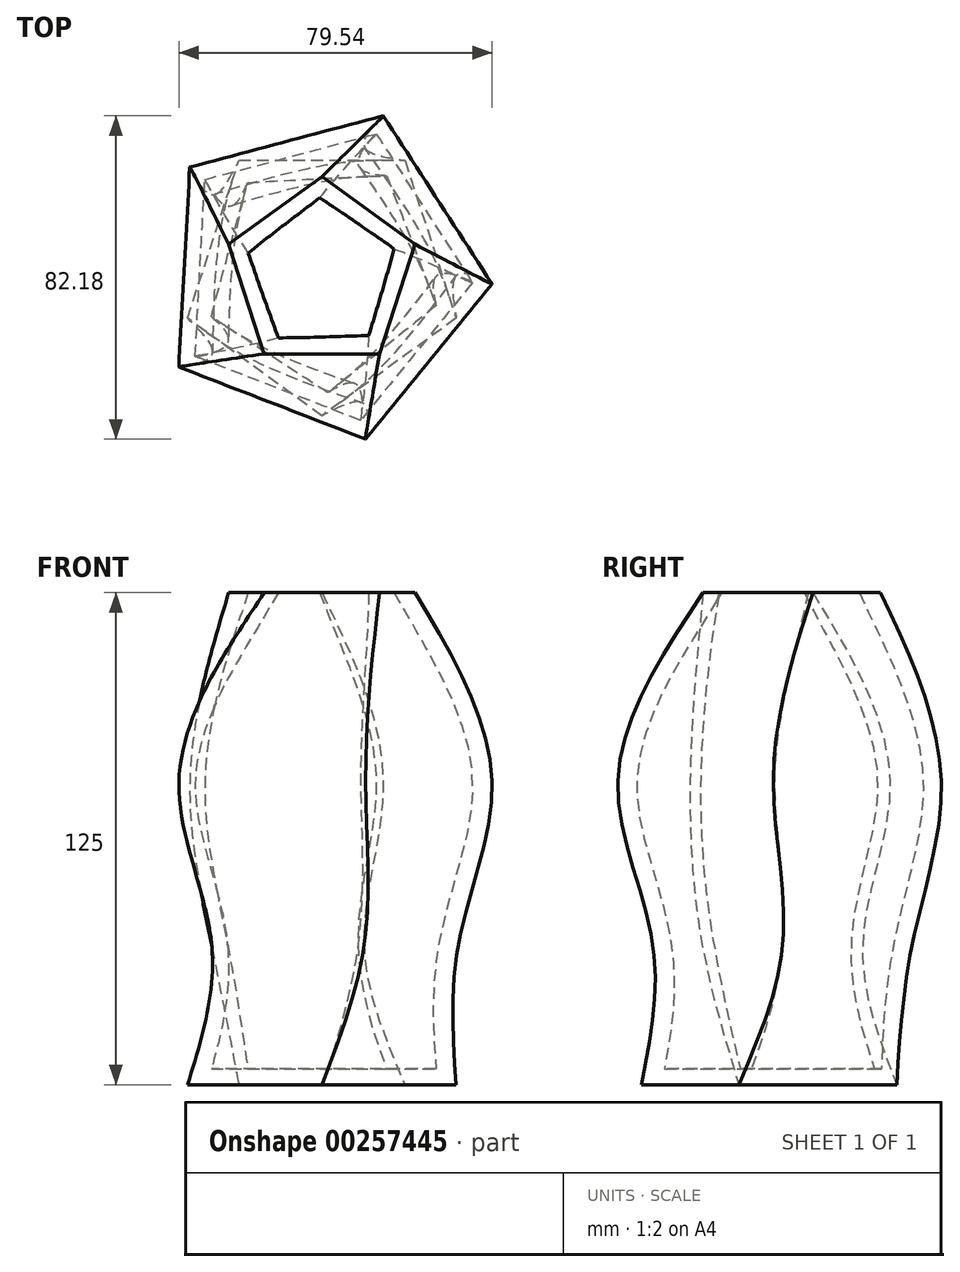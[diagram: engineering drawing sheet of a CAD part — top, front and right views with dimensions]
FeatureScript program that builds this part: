
annotation { "Feature Type Name" : "Feature", "Feature Type Description" : "" }
export const myFeature = defineFeature(function(context is Context, id is Id, definition is map)
    precondition{}
    {
        {
            var Q0;
            Q0=qCreatedBy(makeId("Top.planeOp"),FACE);
            var sketch = newSketch(context, id + "F0", { "sketchPlane" : qUnion([Q0])});
            skCircle(sketch, "E0.cCircle", {"center": v(0, 0) * mm, "radius": 20.14 * mm, "construction": true});
            skLineSegment(sketch, "E0.0", {"start": v(23.68, 7.7) * mm, "end": v(14.63, -20.14) * mm});
            skLineSegment(sketch, "E0.1", {"start": v(14.63, -20.14) * mm, "end": v(-14.63, -20.14) * mm});
            skLineSegment(sketch, "E0.2", {"start": v(-14.63, -20.14) * mm, "end": v(-23.68, 7.7) * mm});
            skLineSegment(sketch, "E0.3", {"start": v(-23.68, 7.7) * mm, "end": v(0, 24.9) * mm});
            skLineSegment(sketch, "E0.4", {"start": v(0, 24.9) * mm, "end": v(23.68, 7.7) * mm});
            skPoint(sketch, "E0.0.midPoint", {"position": v(19.15, -6.22) * mm});
            skSolve(sketch);
        }
        {
            var Q0;
            Q0=qCreatedBy(makeId("Top.planeOp"),FACE);
            cPlane(context, id + "F1", {"entities" : qUnion([Q0]), "cplaneType" : CPlaneType.OFFSET, "offset" : 50 * mm, "oppositeDirection" : true, "width" : 150 * mm, "height" : 150 * mm});
        }
        {
            var Q0;
            Q0=qCreatedBy(id+"F1.planeOp",FACE);
            var sketch = newSketch(context, id + "F2", { "sketchPlane" : qUnion([Q0])});
            skCircle(sketch, "E1.cCircle", {"center": v(0, 0) * mm, "radius": 35 * mm, "construction": true});
            skLineSegment(sketch, "E1.0", {"start": v(15.58, 40.36) * mm, "end": v(43.2, -2.35) * mm});
            skLineSegment(sketch, "E1.1", {"start": v(43.2, -2.35) * mm, "end": v(11.12, -41.8) * mm});
            skLineSegment(sketch, "E1.2", {"start": v(11.12, -41.8) * mm, "end": v(-36.33, -23.5) * mm});
            skLineSegment(sketch, "E1.3", {"start": v(-36.33, -23.5) * mm, "end": v(-33.57, 27.3) * mm});
            skLineSegment(sketch, "E1.4", {"start": v(-33.57, 27.3) * mm, "end": v(15.58, 40.36) * mm});
            skPoint(sketch, "E1.0.midPoint", {"position": v(29.4, 19) * mm});
            skSolve(sketch);
        }
        {
            var Q0;
            Q0=qCreatedBy(id+"F1.planeOp",FACE);
            cPlane(context, id + "F3", {"entities" : qUnion([Q0]), "cplaneType" : CPlaneType.OFFSET, "offset" : 40 * mm, "oppositeDirection" : true, "width" : 150 * mm, "height" : 150 * mm});
        }
        {
            var Q0;
            Q0=qCreatedBy(id+"F3.planeOp",FACE);
            var sketch = newSketch(context, id + "F4", { "sketchPlane" : qUnion([Q0])});
            skCircle(sketch, "E2.cCircle", {"center": v(0, 0) * mm, "radius": 27.95 * mm, "construction": true});
            skLineSegment(sketch, "E2.0", {"start": v(10.68, -32.86) * mm, "end": v(-27.95, -20.3) * mm});
            skLineSegment(sketch, "E2.1", {"start": v(-27.95, -20.3) * mm, "end": v(-27.95, 20.3) * mm});
            skLineSegment(sketch, "E2.2", {"start": v(-27.95, 20.3) * mm, "end": v(10.68, 32.86) * mm});
            skLineSegment(sketch, "E2.3", {"start": v(10.68, 32.86) * mm, "end": v(34.55, 0) * mm});
            skLineSegment(sketch, "E2.4", {"start": v(34.55, 0) * mm, "end": v(10.68, -32.86) * mm});
            skPoint(sketch, "E2.0.midPoint", {"position": v(-8.64, -26.59) * mm});
            skSolve(sketch);
        }
        {
            var Q0;
            Q0=qCreatedBy(id+"F3.planeOp",FACE);
            cPlane(context, id + "F5", {"entities" : qUnion([Q0]), "cplaneType" : CPlaneType.OFFSET, "offset" : 35 * mm, "oppositeDirection" : true, "width" : 150 * mm, "height" : 150 * mm});
        }
        {
            var Q0;
            Q0=qCreatedBy(id+"F5.planeOp",FACE);
            var sketch = newSketch(context, id + "F6", { "sketchPlane" : qUnion([Q0])});
            skCircle(sketch, "E3.cCircle", {"center": v(0, 0) * mm, "radius": 29.03 * mm, "construction": true});
            skLineSegment(sketch, "E3.0", {"start": v(0, -35.88) * mm, "end": v(-34.12, -11.09) * mm});
            skLineSegment(sketch, "E3.1", {"start": v(-34.12, -11.09) * mm, "end": v(-21.1, 29.03) * mm});
            skLineSegment(sketch, "E3.2", {"start": v(-21.1, 29.03) * mm, "end": v(21.1, 29.03) * mm});
            skLineSegment(sketch, "E3.3", {"start": v(21.1, 29.03) * mm, "end": v(34.12, -11.09) * mm});
            skLineSegment(sketch, "E3.4", {"start": v(34.12, -11.09) * mm, "end": v(0, -35.88) * mm});
            skPoint(sketch, "E3.0.midPoint", {"position": v(-17.06, -23.48) * mm});
            skSolve(sketch);
        }
        {
            var Q0;
            Q0=makeQuery(id+"F0.imprint","IMPRINT",FACE,{"disambiguationData":[TD([[makeQuery(id+"F0.imprint","IMPRINT",EDGE,{"derivedFrom":sQuery(id+"F0.wireOp",EDGE,"E0.0")}),-1.0]])]});
            var Q1;
            Q1=makeQuery(id+"F2.imprint","IMPRINT",FACE,{"disambiguationData":[TD([[makeQuery(id+"F2.imprint","IMPRINT",EDGE,{"derivedFrom":sQuery(id+"F2.wireOp",EDGE,"E1.0")}),-1.0]])]});
            var Q2;
            Q2=makeQuery(id+"F4.imprint","IMPRINT",FACE,{"disambiguationData":[TD([[makeQuery(id+"F4.imprint","IMPRINT",EDGE,{"derivedFrom":sQuery(id+"F4.wireOp",EDGE,"E2.0")}),-1.0]])]});
            var Q3;
            Q3=makeQuery(id+"F6.imprint","IMPRINT",FACE,{"disambiguationData":[TD([[makeQuery(id+"F6.imprint","IMPRINT",EDGE,{"derivedFrom":sQuery(id+"F6.wireOp",EDGE,"E3.0")}),-1.0]])]});
            loft(context, id + "F7", {"sheetProfilesArray" : [{ "sheetProfileEntities" : qUnion([Q0]) }, { "sheetProfileEntities" : qUnion([Q1]) }, { "sheetProfileEntities" : qUnion([Q2]) }, { "sheetProfileEntities" : qUnion([Q3]) }]});
        }
        {
            var Q0;
            Q0=makeQuery(id+"F7.opLoft","CAP_FACE",FACE,{"disambiguationData":[OSD([makeQuery(id+"F0.imprint","IMPRINT",FACE,{"disambiguationData":[TD([[makeQuery(id+"F0.imprint","IMPRINT",EDGE,{"derivedFrom":sQuery(id+"F0.wireOp",EDGE,"E0.0")}),-1.0]])]})])],"isStart":true});
            shell(context, id + "F8", {"entities" : qUnion([Q0]), "thickness" : 4 * mm});
        }
    });
